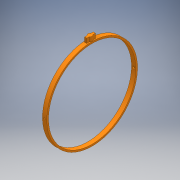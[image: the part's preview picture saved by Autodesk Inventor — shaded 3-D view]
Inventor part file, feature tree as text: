
AUTODESK INVENTOR PART (.ipt)
format: ipt  version: 2018 (Build 220112000, 112)  size: 187,904 bytes
history: native  units: mm
features: extrude x6, plane x6, sketch x6, projected_geometry x3, mirror x2
ambient origin geometry x8: Origin, YZ Plane, XZ Plane, XY Plane, X Axis, Y Axis, Z Axis, Center Point
bodies: Solid1 (feature_tree)
feature tree (23):
  extrude  "Extrusion1"  Depth=204.0mm
  plane  "Work Plane1"
  extrude  "Extrusion2"  Depth=10.0mm
  plane  "Work Plane2"
  extrude  "Extrusion3"  Depth=6.0mm
  mirror  "Mirror1"
  plane  "Work Plane3"
  extrude  "Extrusion4"  Depth=5.0mm TaperAngle=0.0deg
  extrude  "Extrusion5"  Depth=5.0mm
  plane  "Work Plane5"
  extrude  "Extrusion6"  Depth=10.0mm
  mirror  "Mirror2"
  plane  "Work Plane6"
  sketch  "Sketch1"  dims[d0=212.0mm d1=204.0mm]
  sketch  "Sketch2"  dims[d2=10.0mm d3=0.0mm d4=4.0mm]
  projected_geometry  "Projected Loop1"
  sketch  "Sketch3"  dims[d5=227.25mm d6=0.0mm d7=6.0mm]
  sketch  "Sketch4"  dims[d8=5.0mm d9=0.0mm d10=1.0mm d11=0.0mm]
  sketch  "Sketch5"  dims[d12=10.0mm d13=0.0mm d14=5.0mm]
  projected_geometry  "Projected Loop2"
  plane  "Work Plane4"
  sketch  "Sketch6"  dims[d15=12.0mm d16=2.5mm d17=2.5mm d18=12.0mm d19=10.0mm d20=0.0mm]
  projected_geometry  "Projected Loop3"
